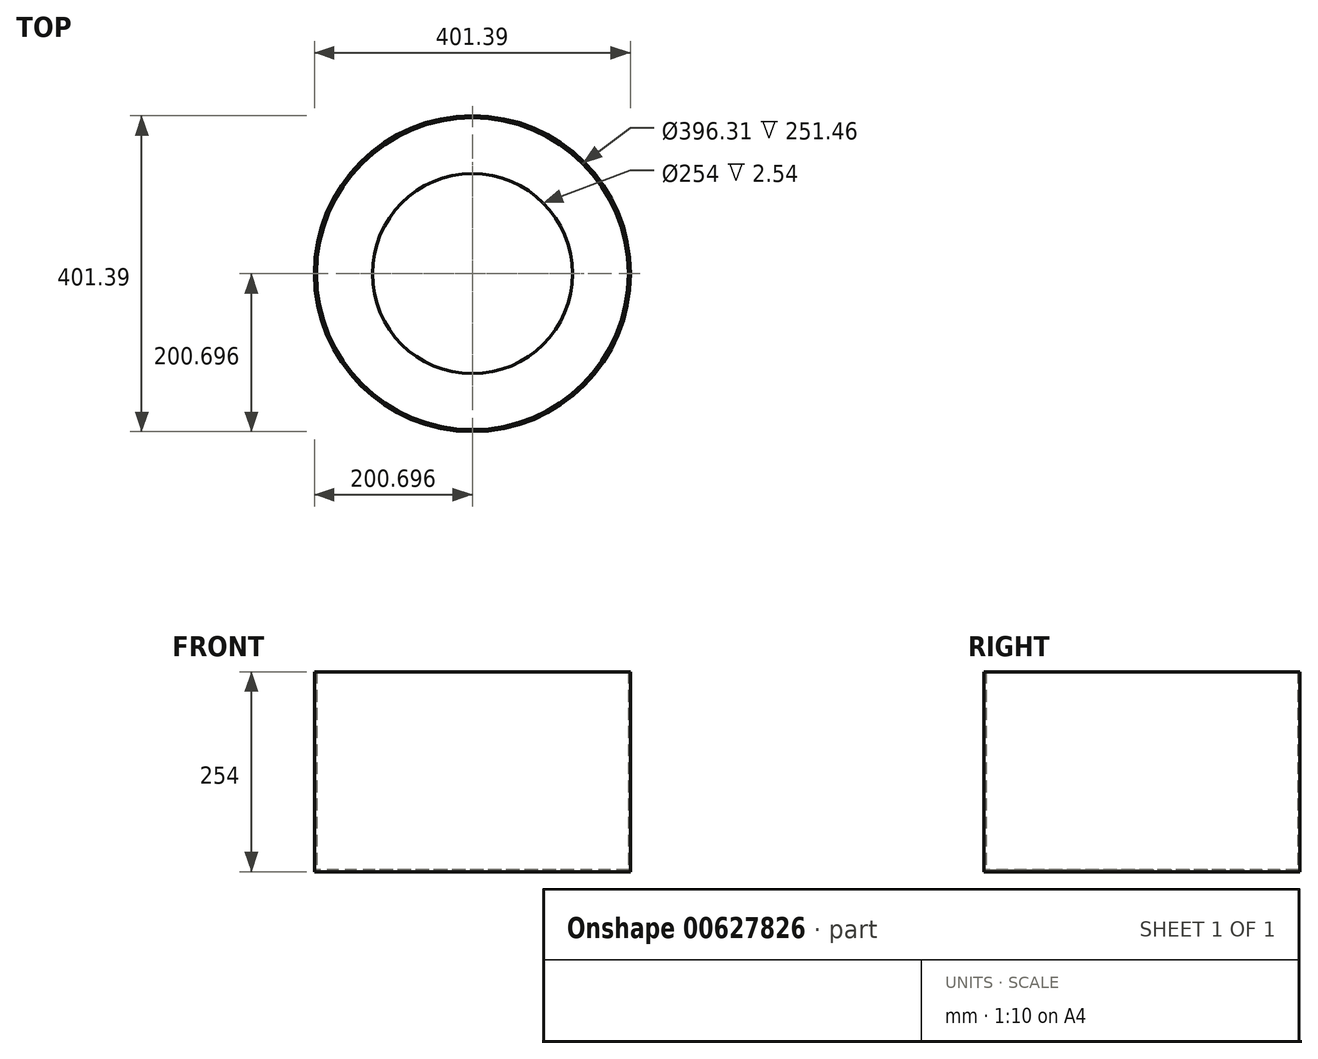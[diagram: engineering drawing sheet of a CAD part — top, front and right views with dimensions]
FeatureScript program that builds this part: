
annotation { "Feature Type Name" : "Feature", "Feature Type Description" : "" }
export const myFeature = defineFeature(function(context is Context, id is Id, definition is map)
    precondition{}
    {
        {
            var Q0;
            Q0=qCreatedBy(makeId("Top.planeOp"),FACE);
            var sketch = newSketch(context, id + "F0", { "sketchPlane" : qUnion([Q0])});
            skCircle(sketch, "E0", {"center": v(-5.85, 9.85) * mm, "radius": 200.7 * mm});
            skSolve(sketch);
        }
        {
            var Q0;
            Q0=makeQuery(id+"F0.imprint","IMPRINT",FACE,{"disambiguationData":[TD([[makeQuery(id+"F0.imprint","IMPRINT",EDGE,{"derivedFrom":sQuery(id+"F0.wireOp",EDGE,"E0")}),1.0]])]});
            extrude(context, id + "F1", {"entities" : qUnion([Q0]), "depth" : 254 * mm, "offsetDistance" : 25.4 * mm});
        }
        {
            var Q0;
            Q0=makeQuery(id+"F1.opExtrude","CAP_FACE",FACE,{"disambiguationData":[OSD([sQuery(id+"F0.wireOp",EDGE,"E0")])],"isStart":false});
            shell(context, id + "F2", {"entities" : qUnion([Q0]), "thickness" : 2.54 * mm});
        }
        {
            var Q0;
            {var subQ0=sQuery(id+"F0.wireOp",EDGE,"E0");Q0=makeQuery(id+"F2.opShell","OFFSET_FACE",FACE,{"disambiguationData":[OSD([subQ0]),TDD([makeQuery(id+"F1.opExtrude","CAP_FACE",FACE,{"disambiguationData":[OSD([subQ0])],"isStart":true})])]});}
            var sketch = newSketch(context, id + "F3", { "sketchPlane" : qUnion([Q0])});
            skPoint(sketch, "E1", {"position": v(-5.85, 9.85) * mm});
            skSolve(sketch);
        }
        {
            var Q0;
            Q0=sQuery(id+"F3.wireOp",VERTEX,"E1");
            var Q1;
            Q1=makeQuery(id+"F1.opExtrude","SWEPT_BODY",BODY,{"disambiguationData":[OSD([sQuery(id+"F0.wireOp",EDGE,"E0")])]});
            hole(context, id + "F4", {"style" : HoleStyle.SIMPLE, "endStyle" : HoleEndStyle.THROUGH, "holeDiameter" : 254 * mm, "majorDiameter" : 6.35 * mm, "isTappedThrough" : true, "tappedDepth" : 12.7 * mm, "tapClearance" : 3, "locations" : qUnion([Q0]), "scope" : qUnion([Q1])});
        }
    });
